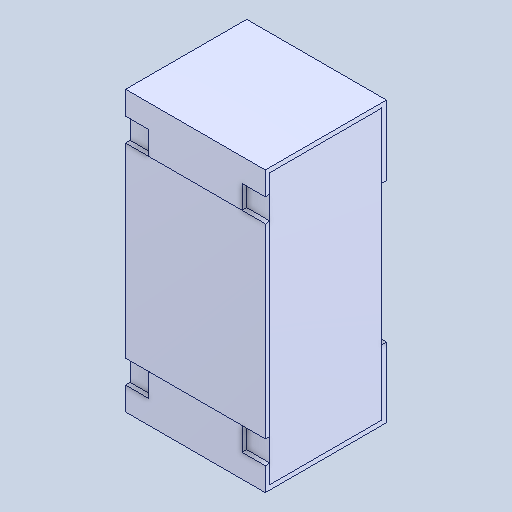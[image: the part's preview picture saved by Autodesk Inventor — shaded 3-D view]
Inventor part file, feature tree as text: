
AUTODESK INVENTOR PART (.ipt)
format: ipt  version: 2025 (Build 290162000, 162)  size: 111,104 bytes
history: native  units: mm
features: boolean_combine x2, other x1, mirror x1
ambient origin geometry x8: Origin, YZ Plane, XZ Plane, XY Plane, X Axis, Y Axis, Z Axis, Center Point
bodies: Solid1 (feature_tree), Solid2 (feature_tree), Solid3 (feature_tree), Solid4 (feature_tree)
feature tree (4):
  other  "Cut-Extrude1"
  boolean_combine  "Combine2"
  mirror  "Mirror1[3]"
  boolean_combine  "Combine1"
